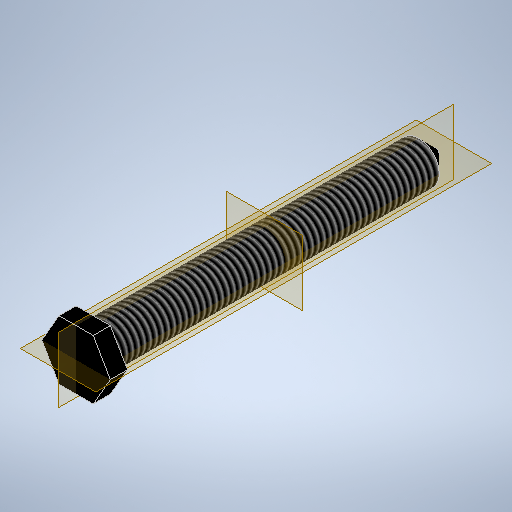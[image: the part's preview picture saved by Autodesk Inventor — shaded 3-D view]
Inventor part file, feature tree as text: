
AUTODESK INVENTOR PART (.ipt)
format: ipt  version: 2025.2 (Build 292293000, 293)  size: 292,352 bytes
history: native  units: mm
features: extrude x2, chamfer x2, sketch x2, other x1, thread x1
ambient origin geometry x8: Origin, YZ Plane, XZ Plane, XY Plane, X Axis, Y Axis, Z Axis, Center Point
bodies: Body1 (feature_tree)
feature tree (8):
  other  "Sólido1"
  extrude  "Extrusão1"  Depth=100.0mm TaperAngle=0.0deg
  extrude  "Extrusão2"  Depth=5.0mm TaperAngle=0.0deg
  thread  "Rosca1"  [1 undecoded]
  chamfer  "Chanfro1"  Distance=2.0mm Angle=45.0deg
  chamfer  "Chanfro2"  Distance=5.0mm Angle=45.0deg
  sketch  "Esboço1"  dims[d0=12.0mm d1=100.0mm d2=0.0mm]
  sketch  "Esboço2"  dims[d3=10.0mm d4=5.0mm d5=0.0mm d6=100.0mm d7=0.0mm d8=2.0mm d9=2.0mm d10=45.0deg d11=5.0mm d12=2.0mm d13=45.0deg]
note: 1 required parameter value undecoded (feature->parameter linkage not recoverable at this tier; creation-order binding heuristic only, values carry confidence <= 0.55)
